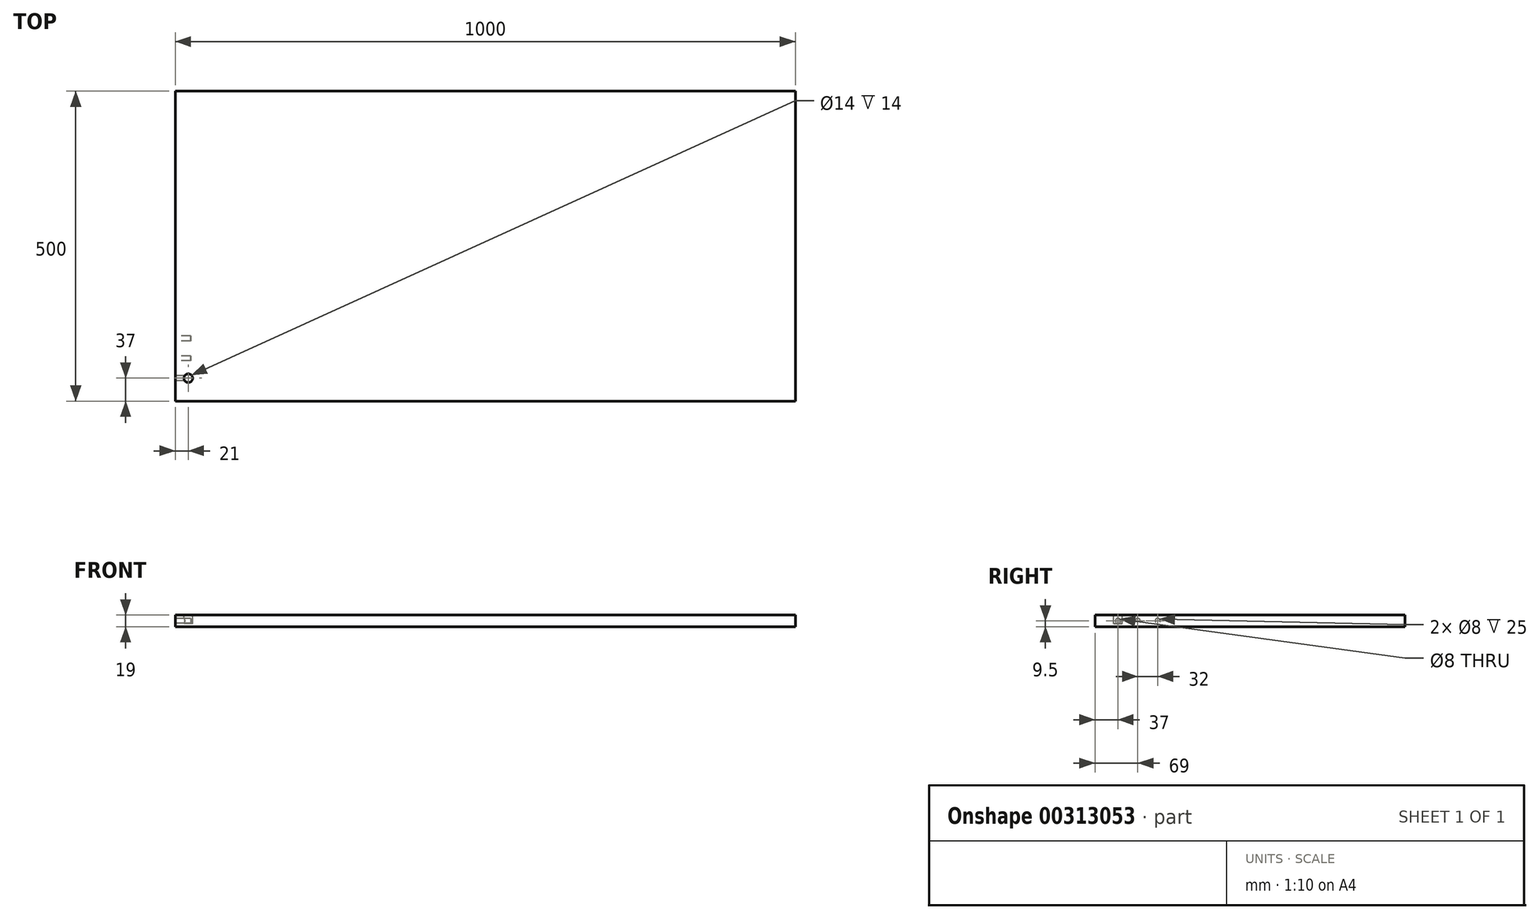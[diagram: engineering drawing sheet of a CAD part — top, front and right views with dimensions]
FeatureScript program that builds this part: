
annotation { "Feature Type Name" : "Feature", "Feature Type Description" : "" }
export const myFeature = defineFeature(function(context is Context, id is Id, definition is map)
    precondition{}
    {
        {
            var Q0;
            Q0=qCreatedBy(makeId("Top.planeOp"),FACE);
            var sketch = newSketch(context, id + "F0", { "sketchPlane" : qUnion([Q0])});
            skLineSegment(sketch, "E0.bottom", {"start": v(500, -250) * mm, "end": v(-500, -250) * mm});
            skLineSegment(sketch, "E0.top", {"start": v(500, 250) * mm, "end": v(-500, 250) * mm});
            skLineSegment(sketch, "E0.left", {"start": v(500, -250) * mm, "end": v(500, 250) * mm});
            skLineSegment(sketch, "E0.right", {"start": v(-500, -250) * mm, "end": v(-500, 250) * mm});
            skPoint(sketch, "E0.middle", {"position": v(0, 0) * mm});
            skSolve(sketch);
        }
        {
            var Q0;
            Q0 = qSketchRegion(id + "F0", true);
            extrude(context, id + "F1", {"entities" : qUnion([Q0]), "depth" : 19 * mm});
        }
        {
            var Q0;
            Q0=makeQuery(id+"F1.opExtrude","CAP_FACE",FACE,{"disambiguationData":[OSD([sQuery(id+"F0.wireOp",EDGE,"E0.bottom"),sQuery(id+"F0.wireOp",EDGE,"E0.top"),sQuery(id+"F0.wireOp",EDGE,"E0.left"),sQuery(id+"F0.wireOp",EDGE,"E0.right")])],"isStart":false});
            var sketch = newSketch(context, id + "F2", { "sketchPlane" : qUnion([Q0])});
            skCircle(sketch, "E1", {"center": v(-479, -213) * mm, "radius": 7 * mm});
            skLineSegment(sketch, "E2", {"start": v(-479, -213) * mm, "end": v(-500, -213) * mm, "construction": true});
            skSolve(sketch);
        }
        {
            var Q0;
            Q0 = qSketchRegion(id + "F2", true);
            extrude(context, id + "F3", {"entities" : qUnion([Q0]), "operationType" : NewBodyOperationType.REMOVE, "oppositeDirection" : true, "depth" : 14 * mm});
        }
        {
            var Q0;
            Q0=makeQuery(id+"F1.opExtrude","SWEPT_FACE",FACE,{"disambiguationData":[OSD([sQuery(id+"F0.wireOp",EDGE,"E0.right")])]});
            var sketch = newSketch(context, id + "F4", { "sketchPlane" : qUnion([Q0])});
            skLineSegment(sketch, "E3", {"start": v(213, 19) * mm, "end": v(213, 0) * mm, "construction": true});
            skCircle(sketch, "E4", {"center": v(213, 9.5) * mm, "radius": 4 * mm});
            skCircle(sketch, "E5.1.0.0", {"center": v(181, 9.5) * mm, "radius": 4 * mm});
            skCircle(sketch, "E5.2.0.0", {"center": v(149, 9.5) * mm, "radius": 4 * mm});
            skLineSegment(sketch, "E5.direction1", {"start": v(213, 9.5) * mm, "end": v(181, 9.5) * mm, "construction": true});
            skSolve(sketch);
        }
        {
            var Q0;
            Q0 = qSketchRegion(id + "F4", true);
            extrude(context, id + "F5", {"entities" : qUnion([Q0]), "operationType" : NewBodyOperationType.REMOVE, "oppositeDirection" : true, "depth" : 25 * mm});
        }
    });
